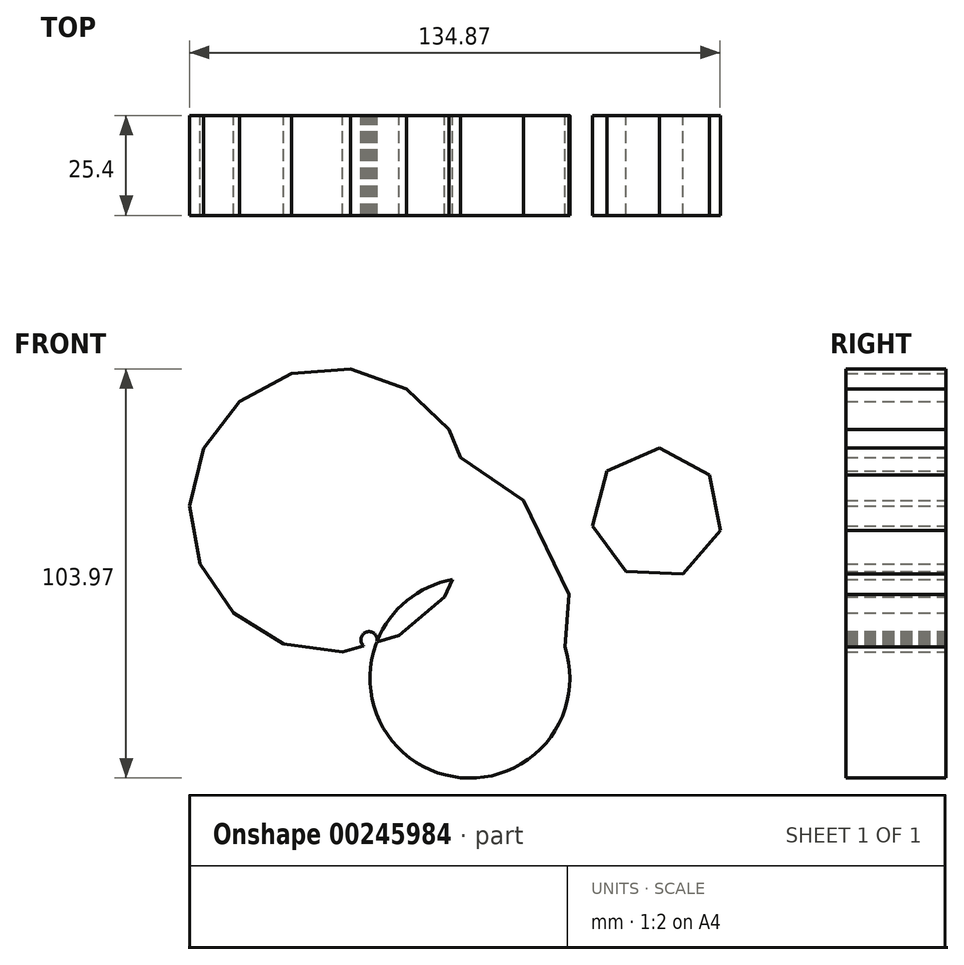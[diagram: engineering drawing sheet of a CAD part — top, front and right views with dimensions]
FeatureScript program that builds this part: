
annotation { "Feature Type Name" : "Feature", "Feature Type Description" : "" }
export const myFeature = defineFeature(function(context is Context, id is Id, definition is map)
    precondition{}
    {
        {
            var Q0;
            Q0=qCreatedBy(makeId("Front.planeOp"),FACE);
            var sketch = newSketch(context, id + "F0", { "sketchPlane" : qUnion([Q0])});
            skCircle(sketch, "E0", {"center": v(0, 0) * mm, "radius": 25.4 * mm});
            skCircle(sketch, "E1.cCircle", {"center": v(-25.64, 9.73) * mm, "radius": 2.07 * mm, "construction": true});
            skLineSegment(sketch, "E1.0", {"start": v(-23.6, 9.4) * mm, "end": v(-23.66, 9.14) * mm});
            skLineSegment(sketch, "E1.1", {"start": v(-23.66, 9.14) * mm, "end": v(-23.75, 8.89) * mm});
            skLineSegment(sketch, "E1.2", {"start": v(-23.75, 8.89) * mm, "end": v(-23.87, 8.65) * mm});
            skLineSegment(sketch, "E1.3", {"start": v(-23.87, 8.65) * mm, "end": v(-24.03, 8.44) * mm});
            skLineSegment(sketch, "E1.4", {"start": v(-24.03, 8.44) * mm, "end": v(-24.2, 8.24) * mm});
            skLineSegment(sketch, "E1.5", {"start": v(-24.2, 8.24) * mm, "end": v(-24.4, 8.07) * mm});
            skLineSegment(sketch, "E1.6", {"start": v(-24.4, 8.07) * mm, "end": v(-24.63, 7.93) * mm});
            skLineSegment(sketch, "E1.7", {"start": v(-24.63, 7.93) * mm, "end": v(-24.87, 7.81) * mm});
            skLineSegment(sketch, "E1.8", {"start": v(-24.87, 7.81) * mm, "end": v(-25.12, 7.73) * mm});
            skLineSegment(sketch, "E1.9", {"start": v(-25.12, 7.73) * mm, "end": v(-25.38, 7.68) * mm});
            skLineSegment(sketch, "E1.10", {"start": v(-25.38, 7.68) * mm, "end": v(-25.65, 7.66) * mm});
            skLineSegment(sketch, "E1.11", {"start": v(-25.65, 7.66) * mm, "end": v(-25.91, 7.68) * mm});
            skLineSegment(sketch, "E1.12", {"start": v(-25.91, 7.68) * mm, "end": v(-26.17, 7.73) * mm});
            skLineSegment(sketch, "E1.13", {"start": v(-26.17, 7.73) * mm, "end": v(-26.43, 7.82) * mm});
            skLineSegment(sketch, "E1.14", {"start": v(-26.43, 7.82) * mm, "end": v(-26.66, 7.93) * mm});
            skLineSegment(sketch, "E1.15", {"start": v(-26.66, 7.93) * mm, "end": v(-26.89, 8.08) * mm});
            skLineSegment(sketch, "E1.16", {"start": v(-26.89, 8.08) * mm, "end": v(-27.09, 8.25) * mm});
            skLineSegment(sketch, "E1.17", {"start": v(-27.09, 8.25) * mm, "end": v(-27.26, 8.45) * mm});
            skLineSegment(sketch, "E1.18", {"start": v(-27.26, 8.45) * mm, "end": v(-27.42, 8.67) * mm});
            skLineSegment(sketch, "E1.19", {"start": v(-27.42, 8.67) * mm, "end": v(-27.54, 8.9) * mm});
            skLineSegment(sketch, "E1.20", {"start": v(-27.54, 8.9) * mm, "end": v(-27.63, 9.15) * mm});
            skLineSegment(sketch, "E1.21", {"start": v(-27.63, 9.15) * mm, "end": v(-27.69, 9.41) * mm});
            skLineSegment(sketch, "E1.22", {"start": v(-27.69, 9.41) * mm, "end": v(-27.71, 9.68) * mm});
            skLineSegment(sketch, "E1.23", {"start": v(-27.71, 9.68) * mm, "end": v(-27.7, 9.94) * mm});
            skLineSegment(sketch, "E1.24", {"start": v(-27.7, 9.94) * mm, "end": v(-27.66, 10.2) * mm});
            skLineSegment(sketch, "E1.25", {"start": v(-27.66, 10.2) * mm, "end": v(-27.58, 10.46) * mm});
            skLineSegment(sketch, "E1.26", {"start": v(-27.58, 10.46) * mm, "end": v(-27.47, 10.7) * mm});
            skLineSegment(sketch, "E1.27", {"start": v(-27.47, 10.7) * mm, "end": v(-27.34, 10.93) * mm});
            skLineSegment(sketch, "E1.28", {"start": v(-27.34, 10.93) * mm, "end": v(-27.17, 11.13) * mm});
            skLineSegment(sketch, "E1.29", {"start": v(-27.17, 11.13) * mm, "end": v(-26.98, 11.32) * mm});
            skLineSegment(sketch, "E1.30", {"start": v(-26.98, 11.32) * mm, "end": v(-26.76, 11.47) * mm});
            skLineSegment(sketch, "E1.31", {"start": v(-26.76, 11.47) * mm, "end": v(-26.53, 11.6) * mm});
            skLineSegment(sketch, "E1.32", {"start": v(-26.53, 11.6) * mm, "end": v(-26.29, 11.7) * mm});
            skLineSegment(sketch, "E1.33", {"start": v(-26.29, 11.7) * mm, "end": v(-26.03, 11.77) * mm});
            skLineSegment(sketch, "E1.34", {"start": v(-26.03, 11.77) * mm, "end": v(-25.77, 11.8) * mm});
            skLineSegment(sketch, "E1.35", {"start": v(-25.77, 11.8) * mm, "end": v(-25.5, 11.8) * mm});
            skLineSegment(sketch, "E1.36", {"start": v(-25.5, 11.8) * mm, "end": v(-25.24, 11.77) * mm});
            skLineSegment(sketch, "E1.37", {"start": v(-25.24, 11.77) * mm, "end": v(-24.98, 11.7) * mm});
            skLineSegment(sketch, "E1.38", {"start": v(-24.98, 11.7) * mm, "end": v(-24.74, 11.6) * mm});
            skLineSegment(sketch, "E1.39", {"start": v(-24.74, 11.6) * mm, "end": v(-24.5, 11.47) * mm});
            skLineSegment(sketch, "E1.40", {"start": v(-24.5, 11.47) * mm, "end": v(-24.3, 11.3) * mm});
            skLineSegment(sketch, "E1.41", {"start": v(-24.3, 11.3) * mm, "end": v(-24.1, 11.12) * mm});
            skLineSegment(sketch, "E1.42", {"start": v(-24.1, 11.12) * mm, "end": v(-23.94, 10.91) * mm});
            skLineSegment(sketch, "E1.43", {"start": v(-23.94, 10.91) * mm, "end": v(-23.8, 10.69) * mm});
            skLineSegment(sketch, "E1.44", {"start": v(-23.8, 10.69) * mm, "end": v(-23.7, 10.44) * mm});
            skLineSegment(sketch, "E1.45", {"start": v(-23.7, 10.44) * mm, "end": v(-23.62, 10.19) * mm});
            skLineSegment(sketch, "E1.46", {"start": v(-23.62, 10.19) * mm, "end": v(-23.58, 9.93) * mm});
            skLineSegment(sketch, "E1.47", {"start": v(-23.58, 9.93) * mm, "end": v(-23.57, 9.66) * mm});
            skLineSegment(sketch, "E1.48", {"start": v(-23.57, 9.66) * mm, "end": v(-23.6, 9.4) * mm});
            skCircle(sketch, "E2.cCircle", {"center": v(-25.24, 11.77) * mm, "radius": 51.25 * mm, "construction": true});
            skLineSegment(sketch, "E2.0", {"start": v(-73.6, 28.73) * mm, "end": v(-58.64, 50.64) * mm});
            skLineSegment(sketch, "E2.1", {"start": v(-58.64, 50.64) * mm, "end": v(-34.73, 62.13) * mm});
            skLineSegment(sketch, "E2.2", {"start": v(-34.73, 62.13) * mm, "end": v(-8.28, 60.13) * mm});
            skLineSegment(sketch, "E2.3", {"start": v(-8.28, 60.13) * mm, "end": v(13.63, 45.17) * mm});
            skLineSegment(sketch, "E2.4", {"start": v(13.63, 45.17) * mm, "end": v(25.13, 21.26) * mm});
            skLineSegment(sketch, "E2.5", {"start": v(25.13, 21.26) * mm, "end": v(23.12, -5.2) * mm});
            skLineSegment(sketch, "E2.6", {"start": v(23.12, -5.2) * mm, "end": v(8.16, -27.1) * mm});
            skLineSegment(sketch, "E2.7", {"start": v(8.16, -27.1) * mm, "end": v(-15.75, -38.6) * mm});
            skLineSegment(sketch, "E2.8", {"start": v(-15.75, -38.6) * mm, "end": v(-42.2, -36.6) * mm});
            skLineSegment(sketch, "E2.9", {"start": v(-42.2, -36.6) * mm, "end": v(-64.1, -21.64) * mm});
            skLineSegment(sketch, "E2.10", {"start": v(-64.1, -21.64) * mm, "end": v(-75.6, 2.27) * mm});
            skLineSegment(sketch, "E2.11", {"start": v(-75.6, 2.27) * mm, "end": v(-73.6, 28.73) * mm});
            skCircle(sketch, "E3.cCircle", {"center": v(47.48, 41.79) * mm, "radius": 16.67 * mm, "construction": true});
            skLineSegment(sketch, "E3.0", {"start": v(31.1, 38.7) * mm, "end": v(34.86, 52.67) * mm});
            skLineSegment(sketch, "E3.1", {"start": v(34.86, 52.67) * mm, "end": v(48.12, 58.44) * mm});
            skLineSegment(sketch, "E3.2", {"start": v(48.12, 58.44) * mm, "end": v(60.9, 51.67) * mm});
            skLineSegment(sketch, "E3.3", {"start": v(60.9, 51.67) * mm, "end": v(63.58, 37.46) * mm});
            skLineSegment(sketch, "E3.4", {"start": v(63.58, 37.46) * mm, "end": v(54.14, 26.5) * mm});
            skLineSegment(sketch, "E3.5", {"start": v(54.14, 26.5) * mm, "end": v(39.68, 27.05) * mm});
            skLineSegment(sketch, "E3.6", {"start": v(39.68, 27.05) * mm, "end": v(31.1, 38.7) * mm});
            skCircle(sketch, "E4.cCircle", {"center": v(-35.14, 42.74) * mm, "radius": 36.16 * mm, "construction": true});
            skLineSegment(sketch, "E4.0", {"start": v(0, 34.19) * mm, "end": v(-6.51, 20.64) * mm});
            skLineSegment(sketch, "E4.1", {"start": v(-6.51, 20.64) * mm, "end": v(-17.98, 10.9) * mm});
            skLineSegment(sketch, "E4.2", {"start": v(-17.98, 10.9) * mm, "end": v(-32.4, 6.68) * mm});
            skLineSegment(sketch, "E4.3", {"start": v(-32.4, 6.68) * mm, "end": v(-47.31, 8.68) * mm});
            skLineSegment(sketch, "E4.4", {"start": v(-47.31, 8.68) * mm, "end": v(-60.1, 16.58) * mm});
            skLineSegment(sketch, "E4.5", {"start": v(-60.1, 16.58) * mm, "end": v(-68.59, 29) * mm});
            skLineSegment(sketch, "E4.6", {"start": v(-68.59, 29) * mm, "end": v(-71.29, 43.8) * mm});
            skLineSegment(sketch, "E4.7", {"start": v(-71.29, 43.8) * mm, "end": v(-67.73, 58.4) * mm});
            skLineSegment(sketch, "E4.8", {"start": v(-67.73, 58.4) * mm, "end": v(-58.54, 70.3) * mm});
            skLineSegment(sketch, "E4.9", {"start": v(-58.54, 70.3) * mm, "end": v(-45.3, 77.44) * mm});
            skLineSegment(sketch, "E4.10", {"start": v(-45.3, 77.44) * mm, "end": v(-30.31, 78.57) * mm});
            skLineSegment(sketch, "E4.11", {"start": v(-30.31, 78.57) * mm, "end": v(-16.15, 73.51) * mm});
            skLineSegment(sketch, "E4.12", {"start": v(-16.15, 73.51) * mm, "end": v(-5.27, 63.13) * mm});
            skLineSegment(sketch, "E4.13", {"start": v(-5.27, 63.13) * mm, "end": v(0.44, 49.22) * mm});
            skLineSegment(sketch, "E4.14", {"start": v(0.44, 49.22) * mm, "end": v(0, 34.19) * mm});
            skSolve(sketch);
        }
        {
            var Q0;
            Q0=makeQuery(id+"F0.imprint","IMPRINT",FACE,{"disambiguationData":[TD([[makeQuery(id+"F0.imprint","IMPRINT",EDGE,{"derivedFrom":sQuery(id+"F0.wireOp",EDGE,"E3.0")}),-1.0]])]});
            var Q1;
            {var subQ0=sQuery(id+"F0.wireOp",EDGE,"E2.5");var subQ1=sQuery(id+"F0.wireOp",EDGE,"E0");var subQ2=makeQuery(id+"F0.imprint","INTERSECT",VERTEX,{"derivedFrom":[subQ1,subQ0]});Q1=makeQuery(id+"F0.imprint","IMPRINT",FACE,{"disambiguationData":[TD([[makeQuery(id+"F0.imprint","IMPRINT",EDGE,{"disambiguationData":[TD([[subQ2,1.0]])],"derivedFrom":subQ1}),1.0]])]});}
            var Q2;
            {var subQ4=sQuery(id+"F0.wireOp",EDGE,"E2.1");Q2=makeQuery(id+"F0.imprint","IMPRINT",FACE,{"disambiguationData":[TD([[makeQuery(id+"F0.imprint","IMPRINT",EDGE,{"derivedFrom":subQ4}),1.0]])]});}
            var Q3;
            {var subQ1=sQuery(id+"F0.wireOp",EDGE,"E2.4");Q3=makeQuery(id+"F0.imprint","IMPRINT",FACE,{"disambiguationData":[TD([[makeQuery(id+"F0.imprint","IMPRINT",EDGE,{"derivedFrom":subQ1}),-1.0]])]});}
            var Q4;
            {var subQ12=sQuery(id+"F0.wireOp",EDGE,"E1.1");Q4=makeQuery(id+"F0.imprint","IMPRINT",FACE,{"disambiguationData":[TD([[makeQuery(id+"F0.imprint","IMPRINT",EDGE,{"derivedFrom":subQ12}),1.0]])]});}
            var Q5;
            {var subQ0=sQuery(id+"F0.wireOp",EDGE,"E1.17");Q5=makeQuery(id+"F0.imprint","IMPRINT",FACE,{"disambiguationData":[TD([[makeQuery(id+"F0.imprint","IMPRINT",EDGE,{"derivedFrom":subQ0}),1.0]])]});}
            extrude(context, id + "F1", {"entities" : qUnion([Q0, Q1, Q2, Q3, Q4, Q5]), "depth" : 25.4 * mm});
        }
    });
